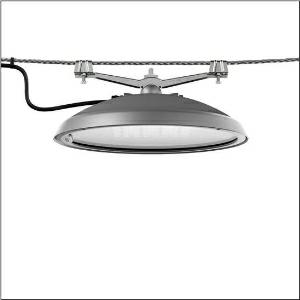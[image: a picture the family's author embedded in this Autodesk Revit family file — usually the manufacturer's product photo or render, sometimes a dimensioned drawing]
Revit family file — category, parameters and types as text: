
# Revit family: dl_r__50_iq_mini___p1_0s_5xa248u41f08ge_754b
name_source: partatom
category: Lighting Fixtures
units: mm (PartAtom-declared; Revit-internal decimal feet)

## family parameters
Cut with Voids When Loaded = No
Host = Face
Light Source = No
Part Type = Normal
Room Calculation Point = No
Round Connector Dimension = Use Diameter
Shared = No

## types (1)
- --- (1 x LED, 5030 lm, 31.2 W, 4000K)
    Apparent Load = 31 VA
    CIE Flux Codes = 23 54 93 100 100
    Color Rendering = 70
    Color Temperature = 4000K
    Default Elevation = 1800 mm
    Description = DL® 50 iQ mini, catenary luminaire, primary light control with lens, of PMMA, primary optical cover: cover, of toughened safety glass, transparent, light distribution: P1.0s, light emission: direct distribution, primary light characteristic: symmetric, installation type: suspended mounting, LED, High Power LED, rated luminous flux: 5.030lm, luminous efficacy: 161lm/W, light colour: 740, colour temperature: 4000K, control gear: iQ Street-Remote, control: optimised constant luminous flux control (CLO 2.0), Desk-Remote (wireless, voltage-free reading and setting of iQ features in the workshop via application-optimized NFC function/RFID function), Light-Fading, Smart-Wire, Night-Set, Lumen-Switch, Temp-Guard, Auto-Match, Street-Remote, mains connection: 230..240V, AC, 50/60Hz, start of lifetime: 31W, end of service life: 32W, reduction: 15W, luminaire housing, of diecast aluminium, powder-coated, Siteco® metallic grey (DB 702S), diameter: 500mm, height: 115mm, mounting height: 4..12m, protection rating (complete): IP66, insulation class (complete): insulation class II (safety insulation), certification: CE, ENEC, ENEC+, VDE, impact resistance: IK08, permissible operating ambient temperature for outdoor applications: -25..+40°C, standard-compliant lighting for roads and squares, packaging unit: 1 piece

Light Distribution: P1.0s
    Height = 124 mm  [stored 0.406824 ft]
    Lamp = 1 x LED
    Lamp Light Flux = 5030 lm
    Lamp Power = 31.2 W
    Lamp count = 1
    Length = 500 mm
    Luminous efficacy = 161 lm/W
    Manufacturer = Siteco
    ModVariant = No
    Model = 5XA248U41F08GE
    Number of Poles = 1
    OnlyDefault = Yes
    Power Factor = 1
    Product Name = DL® 50 iQ mini | P1.0s
    Product group = catenary luminaire
    ProductGroupID = 6300
    Protection Class = Protection class II
    Protection Degree = IP 66
    RLX_Detail_Level = 1
    RLX_Emergency_Light_Flux = 0 lm
    RLX_Emergency_Type = 0
    RLX_Emergency_Type_DB = No
    RlxData = <blob elided: 123381 chars, md5=c987571e>
    Socket = socket
    Standby Power = 0 W
    System Light Flux = 5030 lm
    System Power = 31 W
    Type Comments = factory setting: luminous flux: 100 % | dim-lin: 254 | 325 mA
    Type Image = l_1242791.jpg
    URL = http://relux.com
    VarID = @adj_161663
    Voltage = 0 V
    Weight = 0.00 kg
    Width = 0 mm  [stored 0 ft]

note: [stored X ft] marks values corroborated as IEEE doubles in the binary element streams (Revit-internal decimal feet)

## geometry (parser evidence)
native form markers: Blend x4, Sweep x12
no freeform markers — native parametric forms only
